# Revit family: Gira_5001003
name_source: partatom
category: Electrical Fixtures
revit_build: Autodesk Revit 2017 (Build: 20160225_1515(x64)
units: mm (PartAtom-declared; Revit-internal decimal feet)

## family parameters
Cut with Voids When Loaded = No
Host = Face
Maintain Annotation Orientation = No
Part Type = Normal
Room Calculation Point = No
Round Connector Dimension = Use Diameter
Shared = No

## types (1)
- KNX PB sens.4 Komfort 1-g TS4 white
    BIM = https://media.live.bim.site TS4 1fach.rfa
    BIMSITE_PRODUCT_ID = c639142d951a84f3599d7fd122a1e332b6d742c8
    Bus connection included = Yes
    Colour = White
    Cost = 0 $
    Default Elevation = 1219 mm
    GTIN = 4010337070870
    HAN = 5001003
    HeinzeBIM = https://www.heinze.de
    Manufacturer = Gira
    Number of buttons = 1
    Radio frequent bidirectional = No
    Transparent = No
    URL = https://www.gira.de
    White = White
    With IR sensor = No
    With anti-theft/dismantling protection = Yes
    With display = No
    With label area = No
    With room temperature controller = No

## geometry (parser evidence)
native form markers: Blend x2, Sweep x3
no freeform markers — native parametric forms only
